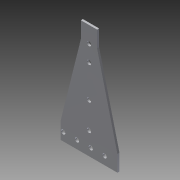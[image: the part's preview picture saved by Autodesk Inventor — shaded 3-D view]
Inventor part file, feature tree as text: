
AUTODESK INVENTOR PART (.ipt)
format: ipt  version: 2013 (Build 170138000, 138)  size: 128,000 bytes
history: native  units: in
note: dims shown in document units (in); Inventor stores cm internally (conversion verified against a paired STEP export)
features: extrude x5, sketch x5, reference x5
ambient origin geometry x8: Origin, YZ Plane, XZ Plane, XY Plane, X Axis, Y Axis, Z Axis, Center Point
bodies: Solid1 (feature_tree)
feature tree (15):
  extrude  "Extrusion1"  Depth=1.0in
  extrude  "Extrusion2"  Depth=1.25in
  extrude  "Extrusion3"  Depth=0.125in
  extrude  "Extrusion4"  Depth=1.0in
  extrude  "Extrusion5"  Depth=0.266in
  sketch  "Sketch1"  dims[d0=7.0in d3=1.0in]
  sketch  "Sketch2"  dims[d4=1.25in d5=1.25in]
  sketch  "Sketch4"  dims[d6=1.0in d7=0.125in]
  reference  "Reference1"
  reference  "Reference2"
  reference  "Reference3"
  reference  "Reference4"
  reference  "Reference5"
  sketch  "Sketch5"  dims[d8=0.125in d9=0.0in d10=1.0in]
  sketch  "Sketch6"  dims[d11=1.0in d12=0.266in d13=0.266in d14=1.0in d15=0.0in d16=1.0in d20=1.0in d21=0.0in d22=2.0in d23=0.266in d24=1.0in d25=0.0in d26=1.625in d27=0.266in d28=1.0in d29=0.0in]
